FCSTD DOCUMENT  (FreeCAD 0.16R)
Label: Mk9Boxy
License: All rights reserved
LicenseURL: http://en.wikipedia.org/wiki/All_rights_reserved
objects: Sketcher::SketchObject×1
note: 1 computed .brp shape members not serialized (recipe doc carries the construction recipe); baked Part::Feature solids carry a one-line shape summary decoded from their .brp

FEATURE [Sketcher::SketchObject] Sketch
  sketch-geometry (14):
    g0: Circle CenterX=489.373 CenterY=335 CenterZ=0 NormalX=0 NormalY=0 NormalZ=1 Radius=335
    g1: Circle CenterX=2261.65 CenterY=250 CenterZ=0 NormalX=0 NormalY=0 NormalZ=1 Radius=250
    g2: Circle CenterX=935.999 CenterY=280 CenterZ=0 NormalX=0 NormalY=0 NormalZ=1 Radius=18
    g3: LineSegment [constr] StartX=935.999 StartY=280 StartZ=0 EndX=1404.61 EndY=949.247 EndZ=0
    g4: LineSegment [constr] StartX=935.999 StartY=280 StartZ=0 EndX=1309.5 EndY=926.921 EndZ=0
    g5: Circle [constr] CenterX=935.999 CenterY=280 CenterZ=0 NormalX=0 NormalY=0 NormalZ=1 Radius=150
    g6: LineSegment StartX=2002.84 StartY=1046.52 StartZ=0 EndX=2261.65 EndY=250 EndZ=0
    g7: LineSegment StartX=2156.48 StartY=573.663 StartZ=0 EndX=2009.5 EndY=426.491 EndZ=0
    g8: LineSegment StartX=2009.5 StartY=426.491 StartZ=0 EndX=2009.5 EndY=150 EndZ=0
    g9: LineSegment StartX=2009.5 StartY=150 StartZ=0 EndX=1209.5 EndY=150 EndZ=0
    g10: LineSegment StartX=1209.5 StartY=150 StartZ=0 EndX=1209.5 EndY=926.921 EndZ=0
    g11: LineSegment StartX=1209.5 StartY=926.921 StartZ=0 EndX=1309.5 EndY=926.921 EndZ=0
    g12: LineSegment [constr] StartX=982.623 StartY=137.43 StartZ=0 EndX=730.23 EndY=909.208 EndZ=0
    g13: LineSegment [constr] StartX=982.623 StartY=137.43 StartZ=0 EndX=800.526 EndY=800.2 EndZ=0
  constraints (34):
    c: Radius(g0) = 335
    c: Radius(g1) = 250
    c: Tangent(g-1,g0)
    c: Tangent(g-1,g1)
    c: Radius(g2) = 18
    c: DistanceY(g2) = 280
    c: Distance(g2,g0) = 450
    c: Coincident(g3,g2)
    c: Coincident(g4,g2)
    c: Distance(g3) = 817
    c: Distance(g4) = 747
    c: Angle(g4) = 1.0472
    c: Angle(g3) = 0.959931
    c: Radius(g5) = 150
    c: Coincident(g5,g2)
    c: Angle(g6) = -1.25664
    c: Coincident(g6,g1)
    c: PointOnObject(g7,g6)
    c: Coincident(g7,g8)
    c: Coincident(g8,g9)
    c: Horizontal(g9)
    c: Coincident(g9,g10)
    c: Vertical(g10)
    c: Distance(g11) = 100
    c: Coincident(g10,g11)
    c: Vertical(g8)
    c: Distance(g9) = 800
    c: Horizontal(g11)
    c: DistanceY(g8) = 150
    c: Coincident(g11,g4)
    c: PointOnObject(g12,g5)
    c: PointOnObject(g2,g12)
    c: Distance(g12) = 812
    c: Coincident(g13,g12)
